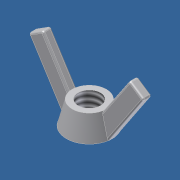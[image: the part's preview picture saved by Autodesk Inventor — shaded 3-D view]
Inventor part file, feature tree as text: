
AUTODESK INVENTOR PART (.ipt)
format: ipt  version: 2011 (Build 150239000, 239)  size: 125,440 bytes
history: native  units: in
note: dims shown in document units (in); Inventor stores cm internally (conversion verified against a paired STEP export)
features: extrude x2, sketch x1, revolve x1, fillet x1, hole x1
ambient origin geometry x8: Origin, YZ Plane, XZ Plane, XY Plane, X Axis, Y Axis, Z Axis, Center Point
bodies: Solid1 (feature_tree)
feature tree (6):
  sketch  "Sketch1"  dims[d0=0.125in d1=0.125in d3=0.15in d4=0.2in d5=0.2in d6=0.2in d8=0.55in d9=0.55in d10=90.0deg d11=0.075in d12=0.0in d13=0.075in d14=0.0in d15=0.015in d16=1.0in d17=1.0in d18=0.196in d19=0.5in d20=0.375in d21=0.25in d22=0.5635in d23=0.75in d24=0.8108in]
  revolve  "Revolution1"  [1 undecoded]
  extrude  "Extrusion1"  Depth=0.15in
  extrude  "Extrusion2"  Depth=0.2in
  fillet  "Fillet1"  Radius=0.2in
  hole  "Hole1"  [1 undecoded]
note: 2 required parameter values undecoded (feature->parameter linkage not recoverable at this tier; creation-order binding heuristic only, values carry confidence <= 0.55)